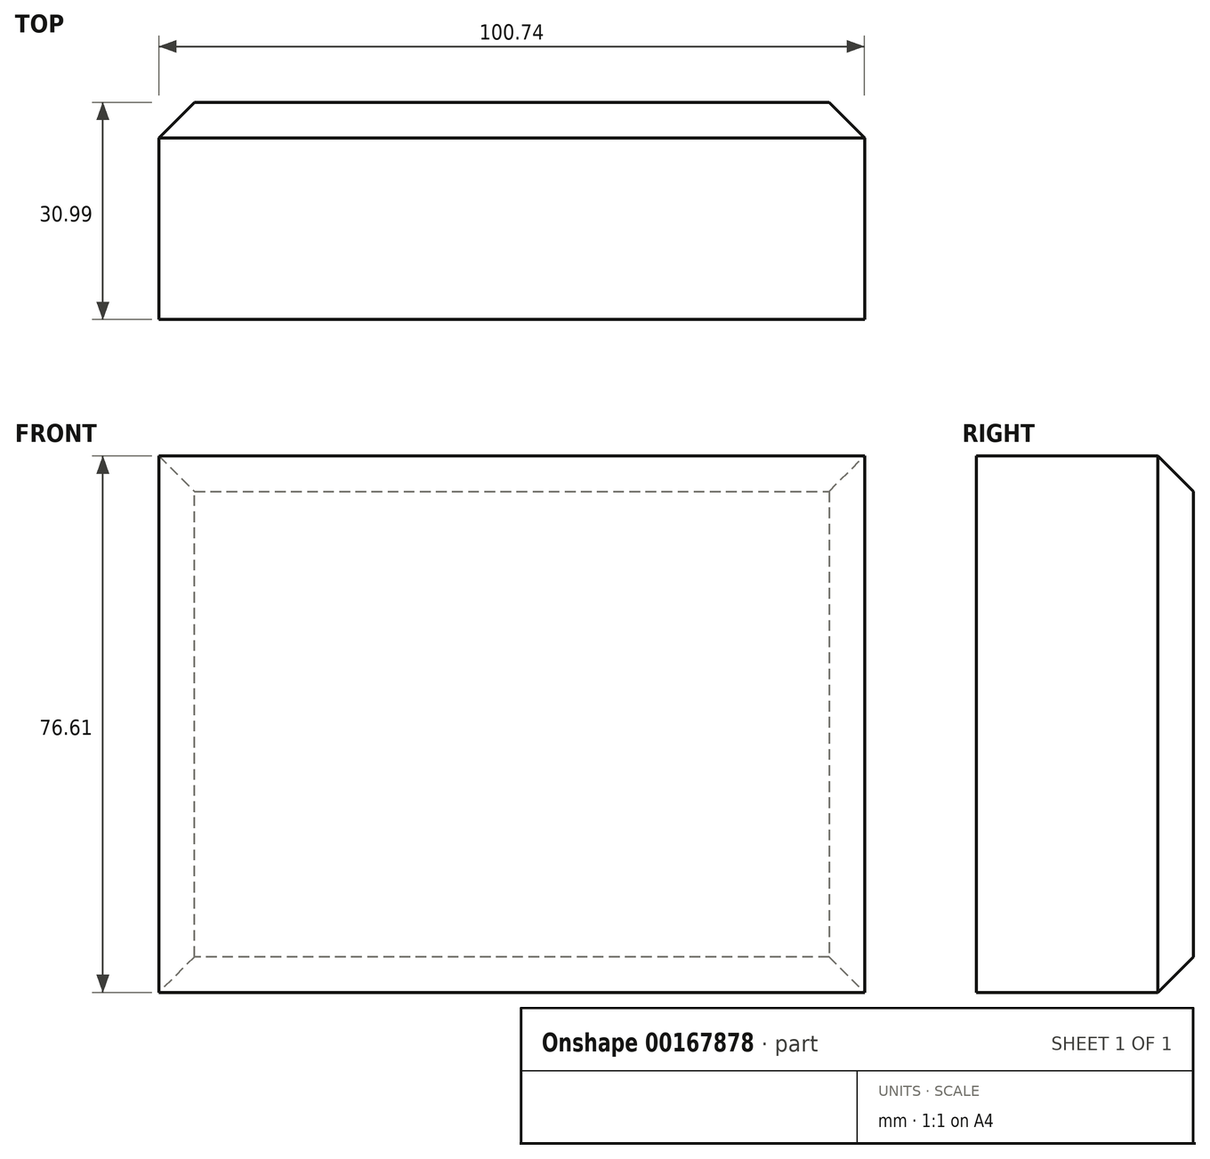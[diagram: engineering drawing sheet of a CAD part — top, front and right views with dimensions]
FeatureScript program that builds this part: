
annotation { "Feature Type Name" : "Feature", "Feature Type Description" : "" }
export const myFeature = defineFeature(function(context is Context, id is Id, definition is map)
    precondition{}
    {
        {
            var Q0;
            Q0=qCreatedBy(makeId("Front.planeOp"),FACE);
            var sketch = newSketch(context, id + "F0", { "sketchPlane" : qUnion([Q0])});
            skLineSegment(sketch, "E0.bottom", {"start": v(-40.53, 39.24) * mm, "end": v(60.21, 39.24) * mm});
            skLineSegment(sketch, "E0.top", {"start": v(-40.53, -37.37) * mm, "end": v(60.21, -37.37) * mm});
            skLineSegment(sketch, "E0.left", {"start": v(-40.53, 39.24) * mm, "end": v(-40.53, -37.37) * mm});
            skLineSegment(sketch, "E0.right", {"start": v(60.21, 39.24) * mm, "end": v(60.21, -37.37) * mm});
            skSolve(sketch);
        }
        {
            var Q0;
            Q0=makeQuery(id+"F0.imprint","IMPRINT",FACE,{"disambiguationData":[TD([[makeQuery(id+"F0.imprint","IMPRINT",EDGE,{"derivedFrom":sQuery(id+"F0.wireOp",EDGE,"E0.bottom")}),-1.0]])]});
            extrude(context, id + "F1", {"entities" : qUnion([Q0]), "oppositeDirection" : true, "depth" : 30.99 * mm});
        }
        {
            var Q0;
            Q0=makeQuery(id+"F1.opExtrude","CAP_EDGE",EDGE,{"disambiguationData":[OSD([sQuery(id+"F0.wireOp",EDGE,"E0.bottom")])],"isStart":false});
            var Q1;
            Q1=makeQuery(id+"F1.opExtrude","CAP_FACE",FACE,{"disambiguationData":[OSD([sQuery(id+"F0.wireOp",EDGE,"E0.bottom"),sQuery(id+"F0.wireOp",EDGE,"E0.top"),sQuery(id+"F0.wireOp",EDGE,"E0.left"),sQuery(id+"F0.wireOp",EDGE,"E0.right")])],"isStart":false});
            chamfer(context, id + "F2", {"entities" : qUnion([Q0, Q1]), "width" : 5.08 * mm, "tangentPropagation" : true});
        }
        {
            var Q0;
            Q0=makeQuery(id+"F1.opExtrude","CAP_FACE",FACE,{"disambiguationData":[OSD([sQuery(id+"F0.wireOp",EDGE,"E0.bottom"),sQuery(id+"F0.wireOp",EDGE,"E0.top"),sQuery(id+"F0.wireOp",EDGE,"E0.left"),sQuery(id+"F0.wireOp",EDGE,"E0.right")])],"isStart":false});
            var sketch = newSketch(context, id + "F3", { "sketchPlane" : qUnion([Q0])});
            skSolve(sketch);
        }
    });
